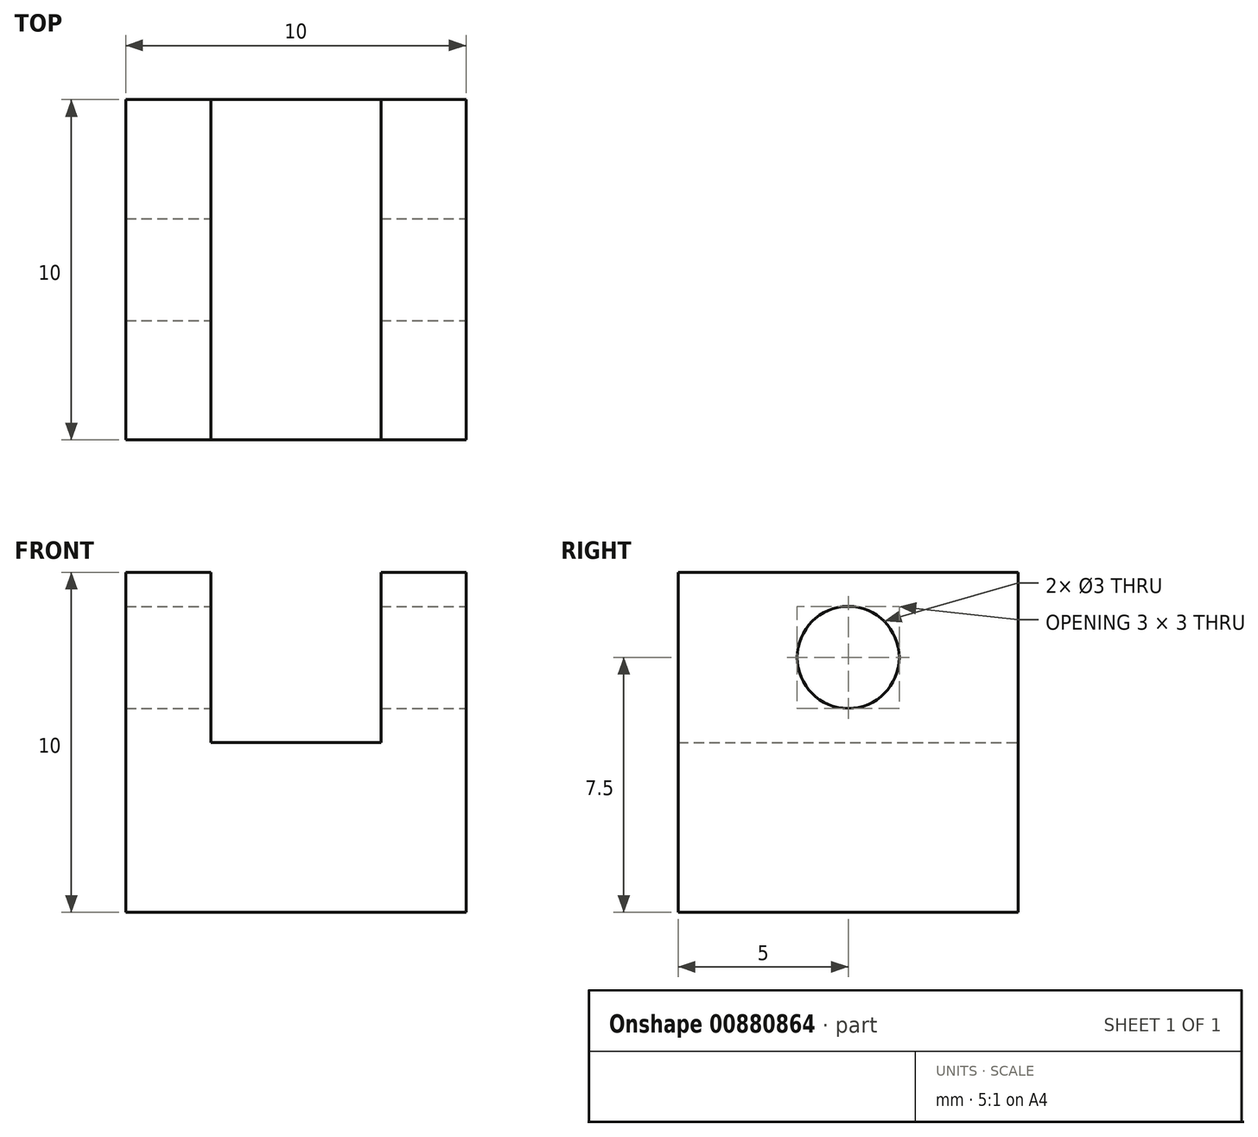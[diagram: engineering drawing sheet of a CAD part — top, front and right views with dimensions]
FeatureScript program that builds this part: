
annotation { "Feature Type Name" : "Feature", "Feature Type Description" : "" }
export const myFeature = defineFeature(function(context is Context, id is Id, definition is map)
    precondition{}
    {
        {
            var Q0;
            Q0=qCreatedBy(makeId("Front.planeOp"),FACE);
            var sketch = newSketch(context, id + "F0", { "sketchPlane" : qUnion([Q0])});
            skLineSegment(sketch, "E0", {"start": v(0, 0) * mm, "end": v(-5, 0) * mm});
            skLineSegment(sketch, "E1", {"start": v(-5, 0) * mm, "end": v(-5, 10) * mm});
            skLineSegment(sketch, "E2", {"start": v(-5, 10) * mm, "end": v(-2.5, 10) * mm});
            skLineSegment(sketch, "E3", {"start": v(-2.5, 10) * mm, "end": v(-2.5, 5) * mm});
            skLineSegment(sketch, "E4", {"start": v(-2.5, 5) * mm, "end": v(0, 5) * mm});
            skLineSegment(sketch, "E5", {"start": v(0, 5) * mm, "end": v(0, 0) * mm});
            skLineSegment(sketch, "E6", {"start": v(0, 0) * mm, "end": v(0, 48.43) * mm, "construction": true});
            skPoint(sketch, "E6.endSnap0", {"position": v(0, 2.5) * mm});
            skLineSegment(sketch, "E7.MirrorCS", {"start": v(5, 0) * mm, "end": v(5, 10) * mm});
            skLineSegment(sketch, "E8.MirrorCS", {"start": v(5, 10) * mm, "end": v(2.5, 10) * mm});
            skLineSegment(sketch, "E9.MirrorCS", {"start": v(2.5, 10) * mm, "end": v(2.5, 5) * mm});
            skLineSegment(sketch, "E10.MirrorCS", {"start": v(2.5, 5) * mm, "end": v(0, 5) * mm});
            skLineSegment(sketch, "E11.MirrorCS", {"start": v(0, 0) * mm, "end": v(5, 0) * mm});
            skSolve(sketch);
        }
        {
            var Q0;
            Q0 = qSketchRegion(id + "F0", true);
            extrude(context, id + "F1", {"entities" : qUnion([Q0]), "endBound" : BoundingType.SYMMETRIC, "depth" : 10 * mm, "offsetDistance" : 25 * mm});
        }
        {
            var Q0;
            Q0=makeQuery(id+"F1.opExtrude","SWEPT_FACE",FACE,{"disambiguationData":[OSD([sQuery(id+"F0.wireOp",EDGE,"E3")])]});
            var sketch = newSketch(context, id + "F2", { "sketchPlane" : qUnion([Q0])});
            skLineSegment(sketch, "E12", {"start": v(0, 10) * mm, "end": v(0, 5) * mm, "construction": true});
            skLineSegment(sketch, "E13", {"start": v(-5, 7.5) * mm, "end": v(5, 7.5) * mm, "construction": true});
            skCircle(sketch, "E14", {"center": v(0, 7.5) * mm, "radius": 1.5 * mm});
            skSolve(sketch);
        }
        {
            var Q0;
            Q0 = qSketchRegion(id + "F2", true);
            extrude(context, id + "F3", {"entities" : qUnion([Q0]), "operationType" : NewBodyOperationType.REMOVE, "endBound" : BoundingType.THROUGH_ALL, "oppositeDirection" : true, "depth" : 25 * mm, "offsetDistance" : 25 * mm, "hasSecondDirection" : true, "secondDirectionBound" : SecondDirectionBoundingType.THROUGH_ALL, "secondDirectionOppositeDirection" : false, "secondDirectionDepth" : 25 * mm});
        }
    });
